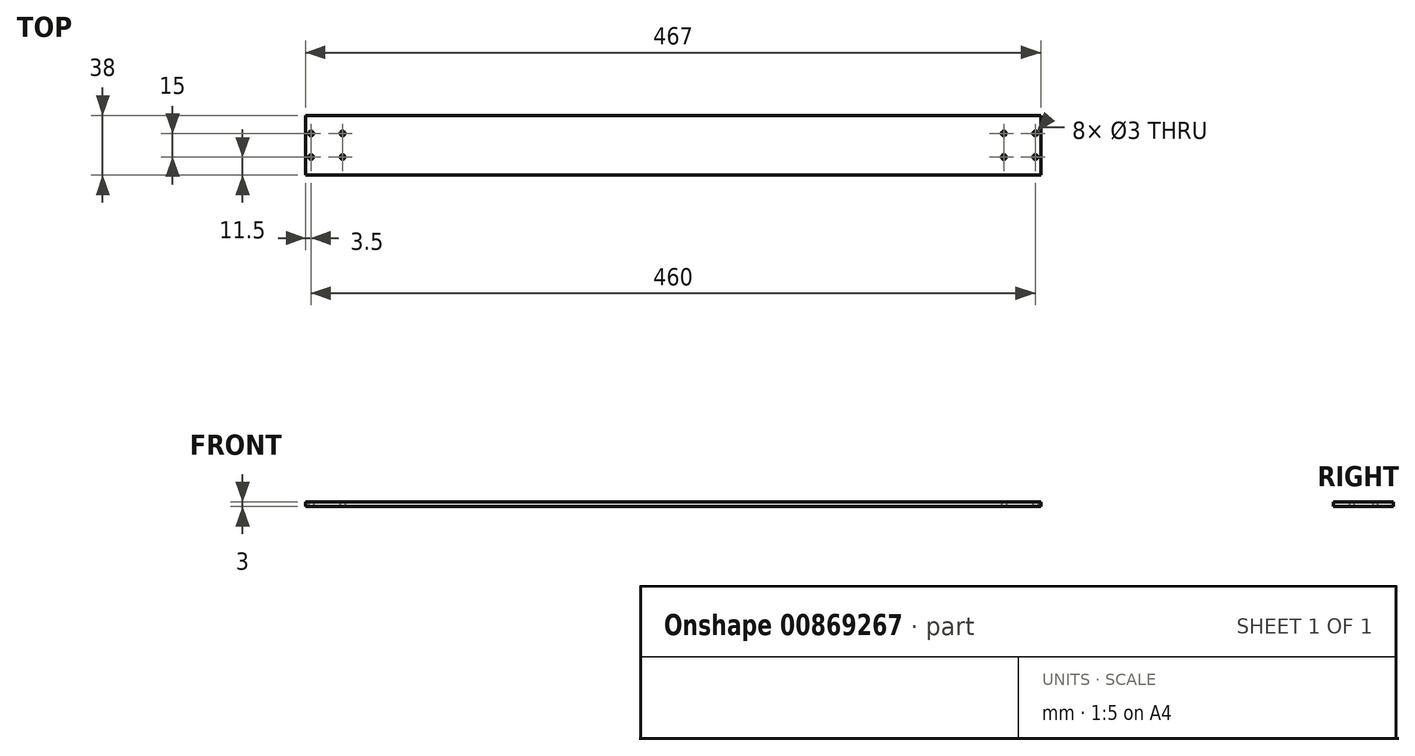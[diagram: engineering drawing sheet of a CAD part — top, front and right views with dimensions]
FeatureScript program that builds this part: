
annotation { "Feature Type Name" : "Feature", "Feature Type Description" : "" }
export const myFeature = defineFeature(function(context is Context, id is Id, definition is map)
    precondition{}
    {
        {
            var Q0;
            Q0=qCreatedBy(makeId("Top.planeOp"),FACE);
            var sketch = newSketch(context, id + "F0", { "sketchPlane" : qUnion([Q0])});
            skLineSegment(sketch, "E0.bottom", {"start": v(233.5, -19) * mm, "end": v(-233.5, -19) * mm});
            skLineSegment(sketch, "E0.top", {"start": v(233.5, 19) * mm, "end": v(-233.5, 19) * mm});
            skLineSegment(sketch, "E0.left", {"start": v(233.5, -19) * mm, "end": v(233.5, 19) * mm});
            skLineSegment(sketch, "E0.right", {"start": v(-233.5, -19) * mm, "end": v(-233.5, 19) * mm});
            skPoint(sketch, "E0.middle", {"position": v(0, 0) * mm});
            skLineSegment(sketch, "E1.bottom", {"start": v(230, -7.5) * mm, "end": v(-230, -7.5) * mm, "construction": true});
            skLineSegment(sketch, "E1.top", {"start": v(230, 7.5) * mm, "end": v(-230, 7.5) * mm, "construction": true});
            skLineSegment(sketch, "E1.left", {"start": v(230, -7.5) * mm, "end": v(230, 7.5) * mm, "construction": true});
            skLineSegment(sketch, "E1.right", {"start": v(-230, -7.5) * mm, "end": v(-230, 7.5) * mm, "construction": true});
            skLineSegment(sketch, "E2.bottom", {"start": v(-210, -7.5) * mm, "end": v(210, -7.5) * mm, "construction": true});
            skLineSegment(sketch, "E2.top", {"start": v(-210, 7.5) * mm, "end": v(210, 7.5) * mm, "construction": true});
            skLineSegment(sketch, "E2.left", {"start": v(-210, -7.5) * mm, "end": v(-210, 7.5) * mm, "construction": true});
            skLineSegment(sketch, "E2.right", {"start": v(210, -7.5) * mm, "end": v(210, 7.5) * mm, "construction": true});
            skSolve(sketch);
        }
        {
            var Q0;
            {var subQ0=sQuery(id+"F0.wireOp",EDGE,"lDbggIsC-9Pjq-ylPt-GzGF-3rXSv8OTqqkK.left");Q0=makeQuery(id+"F0.imprint","IMPRINT",FACE,{"disambiguationData":[TD([[makeQuery(id+"F0.imprint","IMPRINT",EDGE,{"derivedFrom":subQ0}),1.0]])]});}
            var Q1;
            {var subQ0=sQuery(id+"F0.wireOp",EDGE,"lDbggIsC-9Pjq-ylPt-GzGF-3rXSv8OTqqkK.left");Q1=makeQuery(id+"F0.imprint","IMPRINT",FACE,{"disambiguationData":[TD([[makeQuery(id+"F0.imprint","IMPRINT",EDGE,{"derivedFrom":subQ0}),-1.0]])]});}
            var Q2;
            Q2=makeQuery(id+"F0.imprint","IMPRINT",FACE,{"disambiguationData":[TD([[makeQuery(id+"F0.imprint","IMPRINT",EDGE,{"derivedFrom":sQuery(id+"F0.wireOp",EDGE,"E0.bottom")}),-1.0]])]});
            var Q3;
            {var subQ0=sQuery(id+"F0.wireOp",EDGE,"lDbggIsC-9Pjq-ylPt-GzGF-3rXSv8OTqqkK.right");Q3=makeQuery(id+"F0.imprint","IMPRINT",FACE,{"disambiguationData":[TD([[makeQuery(id+"F0.imprint","IMPRINT",EDGE,{"derivedFrom":subQ0}),1.0]])]});}
            var Q4;
            {var subQ0=sQuery(id+"F0.wireOp",EDGE,"E0.left");Q4=makeQuery(id+"F0.imprint","IMPRINT",FACE,{"disambiguationData":[TD([[makeQuery(id+"F0.imprint","IMPRINT",EDGE,{"derivedFrom":subQ0}),1.0]])]});}
            var Q5;
            {var subQ0=sQuery(id+"F0.wireOp",EDGE,"9tgVxiT3-GAhB-J7B1-u8Qe-9STxbGxHfeKx");var subQ1=sQuery(id+"F0.wireOp",EDGE,"E0.top");var subQ2=makeQuery(id+"F0.imprint","INTERSECT",VERTEX,{"derivedFrom":[subQ1,subQ0]});Q5=makeQuery(id+"F0.imprint","IMPRINT",FACE,{"disambiguationData":[TD([[makeQuery(id+"F0.imprint","IMPRINT",EDGE,{"disambiguationData":[TD([[subQ2,-1.0]])],"derivedFrom":subQ1}),1.0]])]});}
            var Q6;
            {var subQ0=sQuery(id+"F0.wireOp",EDGE,"E0.right");Q6=makeQuery(id+"F0.imprint","IMPRINT",FACE,{"disambiguationData":[TD([[makeQuery(id+"F0.imprint","IMPRINT",EDGE,{"derivedFrom":subQ0}),-1.0]])]});}
            var Q7;
            {var subQ0=sQuery(id+"F0.wireOp",EDGE,"kns8efeW-SurV-6yGN-BEES-R5qSqX5v57uJ.right");Q7=makeQuery(id+"F0.imprint","IMPRINT",FACE,{"disambiguationData":[TD([[makeQuery(id+"F0.imprint","IMPRINT",EDGE,{"derivedFrom":subQ0}),1.0]])]});}
            var Q8;
            {var subQ0=sQuery(id+"F0.wireOp",EDGE,"kns8efeW-SurV-6yGN-BEES-R5qSqX5v57uJ.left");Q8=makeQuery(id+"F0.imprint","IMPRINT",FACE,{"disambiguationData":[TD([[makeQuery(id+"F0.imprint","IMPRINT",EDGE,{"derivedFrom":subQ0}),-1.0]])]});}
            var Q9;
            {var subQ0=sQuery(id+"F0.wireOp",EDGE,"lDbggIsC-9Pjq-ylPt-GzGF-3rXSv8OTqqkK.right");Q9=makeQuery(id+"F0.imprint","IMPRINT",FACE,{"disambiguationData":[TD([[makeQuery(id+"F0.imprint","IMPRINT",EDGE,{"derivedFrom":subQ0}),-1.0]])]});}
            var Q10;
            Q10=makeQuery(id+"F0.imprint","IMPRINT",FACE,{"disambiguationData":[TD([[makeQuery(id+"F0.imprint","IMPRINT",EDGE,{"derivedFrom":sQuery(id+"F0.wireOp",EDGE,"yuew3JJc-ggGW-loFv-alUF-mPiGyIKhWcuO.bottom")}),1.0]])]});
            extrude(context, id + "F1", {"entities" : qUnion([Q0, Q1, Q2, Q3, Q4, Q5, Q6, Q7, Q8, Q9, Q10]), "depth" : 3 * mm, "offsetDistance" : 25 * mm});
        }
        {
            var Q0;
            Q0=sQuery(id+"F0.wireOp",VERTEX,"lDbggIsC-9Pjq-ylPt-GzGF-3rXSv8OTqqkK.bottom.start");
            var Q1;
            Q1=sQuery(id+"F0.wireOp",VERTEX,"lDbggIsC-9Pjq-ylPt-GzGF-3rXSv8OTqqkK.top.start");
            var Q2;
            Q2=sQuery(id+"F0.wireOp",VERTEX,"kns8efeW-SurV-6yGN-BEES-R5qSqX5v57uJ.bottom.start");
            var Q3;
            Q3=sQuery(id+"F0.wireOp",VERTEX,"kns8efeW-SurV-6yGN-BEES-R5qSqX5v57uJ.top.start");
            var Q4;
            Q4=sQuery(id+"F0.wireOp",VERTEX,"lDbggIsC-9Pjq-ylPt-GzGF-3rXSv8OTqqkK.bottom.end");
            var Q5;
            Q5=sQuery(id+"F0.wireOp",VERTEX,"lDbggIsC-9Pjq-ylPt-GzGF-3rXSv8OTqqkK.top.end");
            var Q6;
            Q6=sQuery(id+"F0.wireOp",VERTEX,"kns8efeW-SurV-6yGN-BEES-R5qSqX5v57uJ.bottom.end");
            var Q7;
            Q7=sQuery(id+"F0.wireOp",VERTEX,"kns8efeW-SurV-6yGN-BEES-R5qSqX5v57uJ.top.end");
            var Q8;
            Q8=sQuery(id+"F0.wireOp",VERTEX,"SPENIRfS-IH5p-aUrl-JQEh-J2ixLowYmV7N.end");
            var Q9;
            Q9=sQuery(id+"F0.wireOp",VERTEX,"Nj3hFWRa-2wBI-TvjI-A0ed-5YvDgvjEhfMF.end");
            var Q10;
            Q10=sQuery(id+"F0.wireOp",VERTEX,"PRXZggmK-a0Kl-RX5Q-xEX9-M7Xj01d1ijcq.end");
            var Q11;
            Q11=sQuery(id+"F0.wireOp",VERTEX,"9tgVxiT3-GAhB-J7B1-u8Qe-9STxbGxHfeKx.end");
            var Q12;
            Q12=sQuery(id+"F0.wireOp",VERTEX,"clkt58Hp-qifS-NbnN-3gv7-l3VboMF2rrLe.end");
            var Q13;
            Q13=sQuery(id+"F0.wireOp",VERTEX,"clkt58Hp-qifS-NbnN-3gv7-l3VboMF2rrLe.start");
            var Q14;
            Q14=sQuery(id+"F0.wireOp",VERTEX,"cKlAfMTj-mHru-Eo0P-ciV2-PGQHXoxqphZP.end");
            var Q15;
            Q15=sQuery(id+"F0.wireOp",VERTEX,"cKlAfMTj-mHru-Eo0P-ciV2-PGQHXoxqphZP.start");
            var Q16;
            Q16=sQuery(id+"F0.wireOp",VERTEX,"yuew3JJc-ggGW-loFv-alUF-mPiGyIKhWcuO.top.start");
            var Q17;
            Q17=sQuery(id+"F0.wireOp",VERTEX,"yuew3JJc-ggGW-loFv-alUF-mPiGyIKhWcuO.bottom.start");
            var Q18;
            Q18=sQuery(id+"F0.wireOp",VERTEX,"yuew3JJc-ggGW-loFv-alUF-mPiGyIKhWcuO.bottom.end");
            var Q19;
            Q19=sQuery(id+"F0.wireOp",VERTEX,"yuew3JJc-ggGW-loFv-alUF-mPiGyIKhWcuO.top.end");
            var Q20;
            Q20=sQuery(id+"F0.wireOp",VERTEX,"2c85eeb5-ebe2-4795-a89a-680cb6b6d8a1");
            var Q21;
            Q21=sQuery(id+"F0.wireOp",VERTEX,"2fec43f8-824f-41d3-9928-b3adbb108d6f");
            var Q22;
            Q22=sQuery(id+"F0.wireOp",VERTEX,"E1.top.end");
            var Q23;
            Q23=sQuery(id+"F0.wireOp",VERTEX,"E2.top.start");
            var Q24;
            Q24=sQuery(id+"F0.wireOp",VERTEX,"E2.bottom.start");
            var Q25;
            Q25=sQuery(id+"F0.wireOp",VERTEX,"E1.bottom.end");
            var Q26;
            Q26=sQuery(id+"F0.wireOp",VERTEX,"E2.top.end");
            var Q27;
            Q27=sQuery(id+"F0.wireOp",VERTEX,"E1.top.start");
            var Q28;
            Q28=sQuery(id+"F0.wireOp",VERTEX,"E1.bottom.start");
            var Q29;
            Q29=sQuery(id+"F0.wireOp",VERTEX,"E2.bottom.end");
            var Q30;
            Q30=makeQuery(id+"F1.opExtrude","SWEPT_BODY",BODY,{"disambiguationData":[OSD([sQuery(id+"F0.wireOp",EDGE,"E0.bottom"),sQuery(id+"F0.wireOp",EDGE,"E0.top"),sQuery(id+"F0.wireOp",EDGE,"E0.left"),sQuery(id+"F0.wireOp",EDGE,"E0.right"),sQuery(id+"F0.wireOp",EDGE,"lDbggIsC-9Pjq-ylPt-GzGF-3rXSv8OTqqkK.right"),sQuery(id+"F0.wireOp",EDGE,"kns8efeW-SurV-6yGN-BEES-R5qSqX5v57uJ.bottom"),sQuery(id+"F0.wireOp",EDGE,"kns8efeW-SurV-6yGN-BEES-R5qSqX5v57uJ.top"),sQuery(id+"F0.wireOp",EDGE,"kns8efeW-SurV-6yGN-BEES-R5qSqX5v57uJ.right")])]});
            hole(context, id + "F2", {"style" : HoleStyle.SIMPLE, "endStyle" : HoleEndStyle.THROUGH, "oppositeDirection" : true, "holeDiameter" : 3 * mm, "majorDiameter" : 5 * mm, "isTappedThrough" : true, "tappedDepth" : 12 * mm, "tapClearance" : 3, "locations" : qUnion([Q0, Q1, Q2, Q3, Q4, Q5, Q6, Q7, Q8, Q9, Q10, Q11, Q12, Q13, Q14, Q15, Q16, Q17, Q18, Q19, Q20, Q21, Q22, Q23, Q24, Q25, Q26, Q27, Q28, Q29]), "scope" : qUnion([Q30])});
        }
    });
